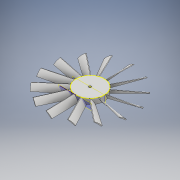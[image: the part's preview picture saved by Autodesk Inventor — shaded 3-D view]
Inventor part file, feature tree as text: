
AUTODESK INVENTOR PART (.ipt)
format: ipt  version: 2018 (Build 220112000, 112)  size: 343,040 bytes
history: native  units: mm
features: sketch x5, extrude x2, plane x2, sweep x1, pattern_circular x1
ambient origin geometry x8: Origin, YZ Plane, XZ Plane, XY Plane, X Axis, Y Axis, Z Axis, Center Point
bodies: Solid1 (feature_tree)
feature tree (11):
  extrude  "Extrusion1"  Depth=25.0mm
  sketch  "Sketch2"  dims[d3=2.0mm d4=2.0mm]
  plane  "Work Plane1"
  sweep  "Sweep1"
  extrude  "Extrusion2"  Depth=25.0mm
  pattern_circular  "Circular Pattern1"  Count=14 Angle=360.0deg
  plane  "Work Plane3"
  sketch  "Sketch1"  dims[d0=2.25mm d1=25.0mm]
  sketch  "Sketch3"  dims[d5=5.0mm d6=0.0mm d13=25.0mm]
  sketch  "Sketch5"  dims[d14=0.0mm d15=3.490659mm]
  sketch  "Sketch6"  dims[d16=1.0mm d17=0.0mm d18=140.0mm d19=360.0deg d21=12.5mm]
